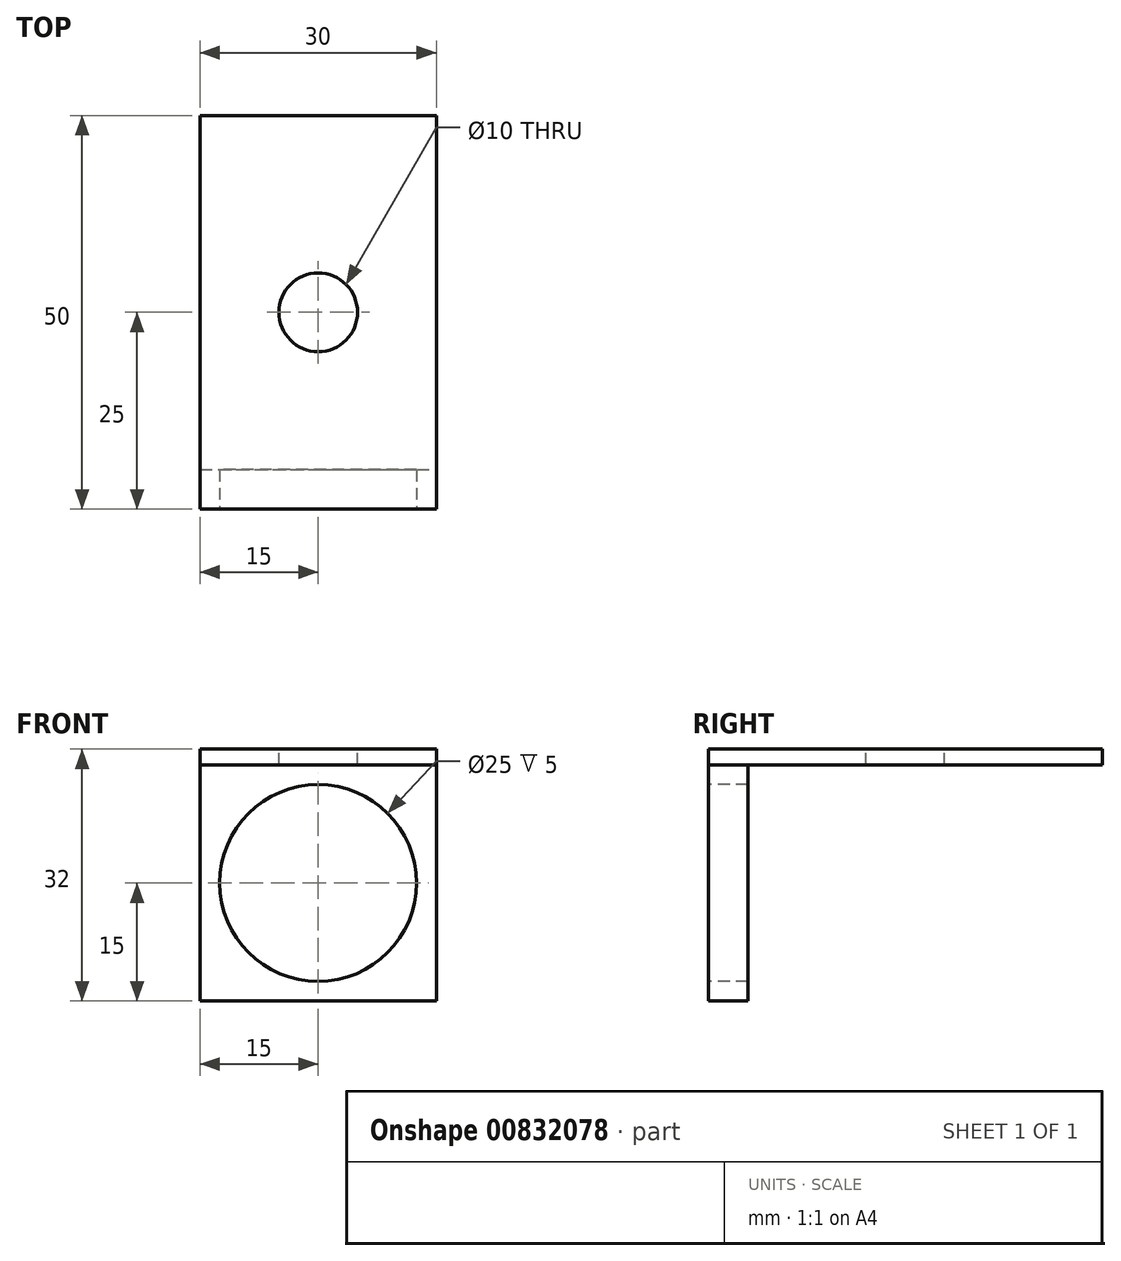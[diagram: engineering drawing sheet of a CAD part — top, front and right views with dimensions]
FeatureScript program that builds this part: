
annotation { "Feature Type Name" : "Feature", "Feature Type Description" : "" }
export const myFeature = defineFeature(function(context is Context, id is Id, definition is map)
    precondition{}
    {
        {
            var Q0;
            Q0=qCreatedBy(makeId("Front.planeOp"),FACE);
            var sketch = newSketch(context, id + "F0", { "sketchPlane" : qUnion([Q0])});
            skLineSegment(sketch, "E0.bottom", {"start": v(-15, 2) * mm, "end": v(15, 2) * mm});
            skLineSegment(sketch, "E0.top", {"start": v(-15, 0) * mm, "end": v(15, 0) * mm});
            skLineSegment(sketch, "E0.left", {"start": v(-15, 2) * mm, "end": v(-15, 0) * mm});
            skLineSegment(sketch, "E0.right", {"start": v(15, 2) * mm, "end": v(15, 0) * mm});
            skSolve(sketch);
        }
        {
            var Q0;
            Q0 = qSketchRegion(id + "F0", true);
            extrude(context, id + "F1", {"entities" : qUnion([Q0]), "endBound" : BoundingType.SYMMETRIC, "depth" : 50 * mm, "offsetDistance" : 25 * mm});
        }
        {
            var Q0;
            Q0=makeQuery(id+"F1.opExtrude","SWEPT_FACE",FACE,{"disambiguationData":[OSD([sQuery(id+"F0.wireOp",EDGE,"E0.bottom")])]});
            var sketch = newSketch(context, id + "F2", { "sketchPlane" : qUnion([Q0])});
            skCircle(sketch, "E1", {"center": v(0, 0) * mm, "radius": 5 * mm});
            skSolve(sketch);
        }
        {
            var Q0;
            Q0 = qSketchRegion(id + "F2", true);
            extrude(context, id + "F3", {"entities" : qUnion([Q0]), "operationType" : NewBodyOperationType.REMOVE, "endBound" : BoundingType.THROUGH_ALL, "oppositeDirection" : true, "depth" : 25 * mm, "offsetDistance" : 25 * mm});
        }
        {
            var Q0;
            Q0=makeQuery(id+"F1.opExtrude","SWEPT_FACE",FACE,{"disambiguationData":[OSD([sQuery(id+"F0.wireOp",EDGE,"E0.top")])]});
            var sketch = newSketch(context, id + "F4", { "sketchPlane" : qUnion([Q0])});
            skLineSegment(sketch, "E2.bottom", {"start": v(-15, 25) * mm, "end": v(15, 25) * mm});
            skLineSegment(sketch, "E2.top", {"start": v(-15, 20) * mm, "end": v(15, 20) * mm});
            skLineSegment(sketch, "E2.left", {"start": v(-15, 25) * mm, "end": v(-15, 20) * mm});
            skLineSegment(sketch, "E2.right", {"start": v(15, 25) * mm, "end": v(15, 20) * mm});
            skSolve(sketch);
        }
        {
            var Q0;
            Q0 = qSketchRegion(id + "F4", true);
            extrude(context, id + "F5", {"entities" : qUnion([Q0]), "depth" : 30 * mm, "offsetDistance" : 25 * mm});
        }
        {
            var Q0;
            Q0=makeQuery(id+"F5.opExtrude","SWEPT_FACE",FACE,{"disambiguationData":[OSD([sQuery(id+"F4.wireOp",EDGE,"E2.bottom")])]});
            var sketch = newSketch(context, id + "F6", { "sketchPlane" : qUnion([Q0])});
            skCircle(sketch, "E3", {"center": v(0, -15) * mm, "radius": 12.5 * mm});
            skLineSegment(sketch, "E4", {"start": v(15, 0) * mm, "end": v(-15, -30) * mm, "construction": true});
            skSolve(sketch);
        }
        {
            var Q0;
            Q0 = qSketchRegion(id + "F6", true);
            extrude(context, id + "F7", {"entities" : qUnion([Q0]), "operationType" : NewBodyOperationType.REMOVE, "endBound" : BoundingType.THROUGH_ALL, "oppositeDirection" : true, "depth" : 25 * mm, "offsetDistance" : 25 * mm});
        }
    });
